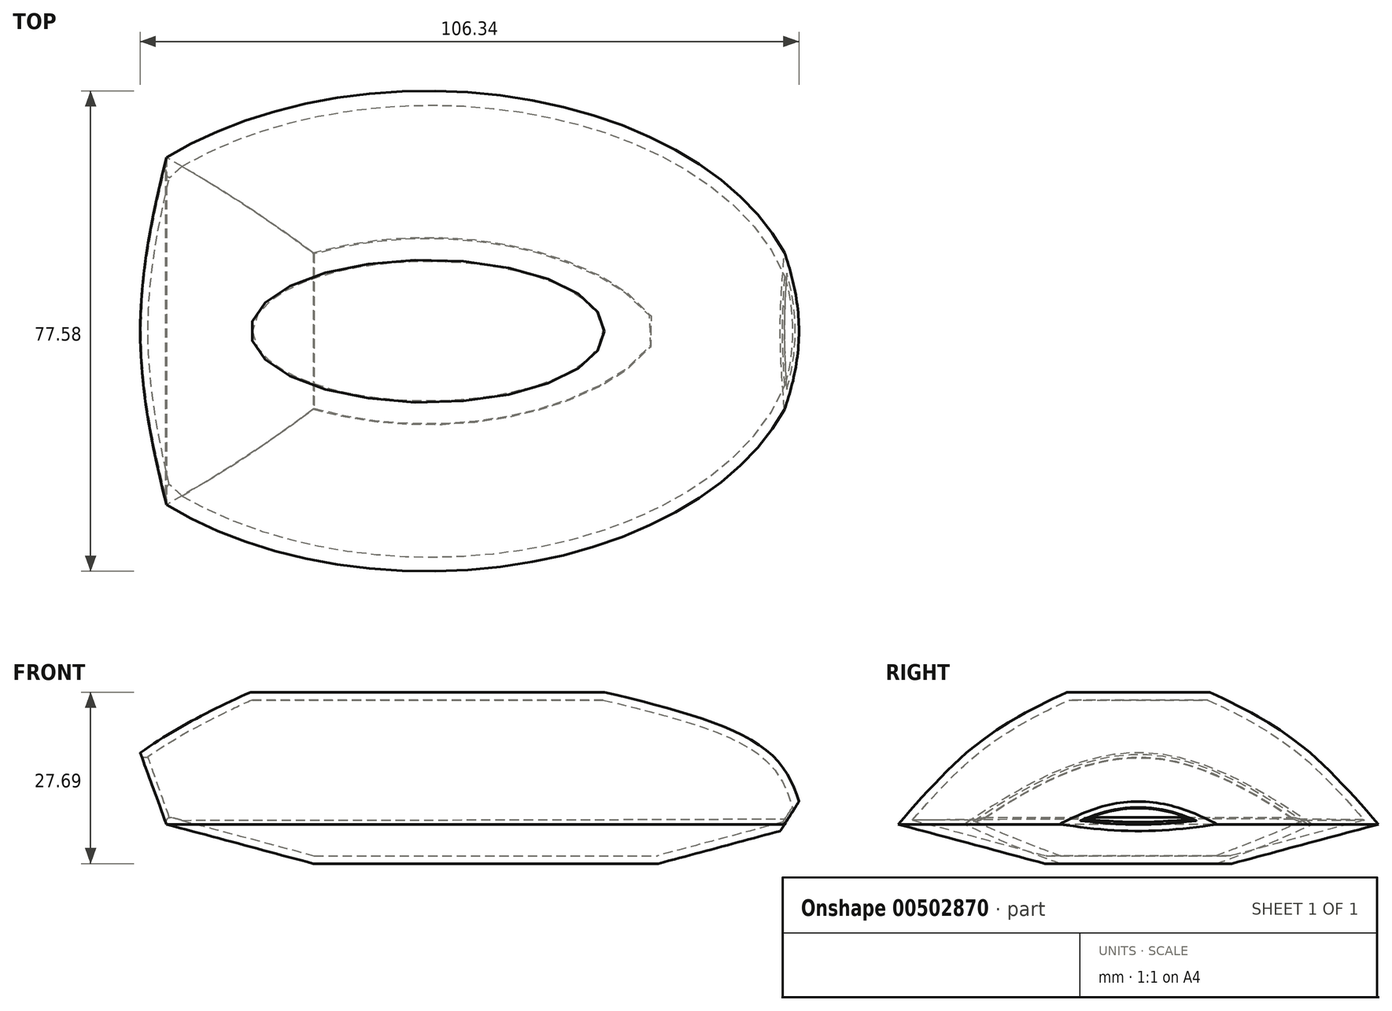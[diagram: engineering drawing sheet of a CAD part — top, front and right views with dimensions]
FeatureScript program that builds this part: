
annotation { "Feature Type Name" : "Feature", "Feature Type Description" : "" }
export const myFeature = defineFeature(function(context is Context, id is Id, definition is map)
    precondition{}
    {
        {
            var Q0;
            Q0=qCreatedBy(makeId("Top.planeOp"),FACE);
            var sketch = newSketch(context, id + "F0", { "sketchPlane" : qUnion([Q0])});
            skEllipse(sketch, "E0", {"center": v(0, 0) * mm, "majorRadius": 60.99 * mm, "minorRadius": 38.8 * mm, "majorAxis": v(1, 0)});
            skSolve(sketch);
        }
        {
            var Q0;
            Q0=qCreatedBy(makeId("Top.planeOp"),FACE);
            cPlane(context, id + "F1", {"entities" : qUnion([Q0]), "cplaneType" : CPlaneType.OFFSET, "offset" : 11.43 * mm, "width" : 152.4 * mm, "height" : 152.4 * mm});
        }
        {
            var Q0;
            Q0=qCreatedBy(id+"F1.planeOp",FACE);
            var sketch = newSketch(context, id + "F2", { "sketchPlane" : qUnion([Q0])});
            skEllipse(sketch, "E1", {"center": v(4.4, 0) * mm, "majorRadius": 50.93 * mm, "minorRadius": 27.86 * mm, "majorAxis": v(1, 0)});
            skSolve(sketch);
        }
        {
            var Q0;
            Q0=qCreatedBy(id+"F1.planeOp",FACE);
            cPlane(context, id + "F3", {"entities" : qUnion([Q0]), "cplaneType" : CPlaneType.OFFSET, "offset" : 9.9 * mm, "width" : 152.4 * mm, "height" : 152.4 * mm});
        }
        {
            var Q0;
            Q0=qCreatedBy(id+"F3.planeOp",FACE);
            var sketch = newSketch(context, id + "F4", { "sketchPlane" : qUnion([Q0])});
            skEllipse(sketch, "E2", {"center": v(0, 0) * mm, "majorRadius": 28.55 * mm, "minorRadius": 11.52 * mm, "majorAxis": v(1, 0)});
            skSolve(sketch);
        }
        {
            var Q0;
            Q0=makeQuery(id+"F0.imprint","IMPRINT",FACE,{"disambiguationData":[TD([[makeQuery(id+"F0.imprint","IMPRINT",EDGE,{"derivedFrom":sQuery(id+"F0.wireOp",EDGE,"E0")}),1.0]])]});
            var Q1;
            Q1=makeQuery(id+"F2.imprint","IMPRINT",FACE,{"disambiguationData":[TD([[makeQuery(id+"F2.imprint","IMPRINT",EDGE,{"derivedFrom":sQuery(id+"F2.wireOp",EDGE,"E1")}),1.0]])]});
            var Q2;
            Q2=makeQuery(id+"F4.imprint","IMPRINT",FACE,{"disambiguationData":[TD([[makeQuery(id+"F4.imprint","IMPRINT",EDGE,{"derivedFrom":sQuery(id+"F4.wireOp",EDGE,"E2")}),1.0]])]});
            loft(context, id + "F5", {"sheetProfilesArray" : [{ "sheetProfileEntities" : qUnion([Q0]) }, { "sheetProfileEntities" : qUnion([Q1]) }, { "sheetProfileEntities" : qUnion([Q2]) }]});
        }
        {
            var Q0;
            Q0=qCreatedBy(makeId("Front.planeOp"),FACE);
            var sketch = newSketch(context, id + "F6", { "sketchPlane" : qUnion([Q0])});
            skLineSegment(sketch, "E3", {"start": v(-50.93, 24.05) * mm, "end": v(-38.98, -8.65) * mm});
            skLineSegment(sketch, "E4", {"start": v(-38.98, -8.65) * mm, "end": v(-67.9, -14.93) * mm});
            skLineSegment(sketch, "E5", {"start": v(-67.9, -14.93) * mm, "end": v(-64.13, 29.08) * mm});
            skLineSegment(sketch, "E6", {"start": v(-64.13, 29.08) * mm, "end": v(-50.93, 24.05) * mm});
            skSolve(sketch);
        }
        {
            var Q0;
            Q0 = qSketchRegion(id + "F6", true);
            extrude(context, id + "F7", {"entities" : qUnion([Q0]), "operationType" : NewBodyOperationType.REMOVE, "endBound" : BoundingType.SYMMETRIC, "oppositeDirection" : true, "depth" : 172.72 * mm, "offsetDistance" : 25.4 * mm});
        }
        {
            var Q0;
            Q0=makeQuery(id+"F5.opLoft","CAP_FACE",FACE,{"disambiguationData":[OSD([makeQuery(id+"F0.imprint","IMPRINT",FACE,{"disambiguationData":[TD([[makeQuery(id+"F0.imprint","IMPRINT",EDGE,{"derivedFrom":sQuery(id+"F0.wireOp",EDGE,"E0")}),1.0]])]})])],"isStart":true});
            extrude(context, id + "F8", {"entities" : qUnion([Q0]), "operationType" : NewBodyOperationType.ADD, "depth" : 6.35 * mm, "offsetDistance" : 25.4 * mm, "hasDraft" : true, "draftAngle" : 75 * degree, "draftPullDirection" : true});
        }
        {
            var Q0;
            Q0=qCreatedBy(makeId("Front.planeOp"),FACE);
            var sketch = newSketch(context, id + "F9", { "sketchPlane" : qUnion([Q0])});
            skLineSegment(sketch, "E7", {"start": v(64.03, 10.07) * mm, "end": v(51.06, -10.4) * mm});
            skLineSegment(sketch, "E8", {"start": v(51.06, -10.4) * mm, "end": v(65.19, -14.72) * mm});
            skLineSegment(sketch, "E9", {"start": v(65.19, -14.72) * mm, "end": v(64.03, 10.07) * mm});
            skSolve(sketch);
        }
        {
            var Q0;
            Q0 = qSketchRegion(id + "F9", true);
            extrude(context, id + "F10", {"entities" : qUnion([Q0]), "operationType" : NewBodyOperationType.REMOVE, "endBound" : BoundingType.SYMMETRIC, "oppositeDirection" : true, "depth" : 77.22 * mm, "offsetDistance" : 25.4 * mm});
        }
        {
            var Q0;
            Q0=makeQuery(id+"F7.boolean.opBoolean","COPY",FACE,{"derivedFrom":makeQuery(id+"F7.opExtrude","SWEPT_FACE",FACE,{"disambiguationData":[OSD([sQuery(id+"F6.wireOp",EDGE,"E3")])]})});
            var Q1;
            Q1=makeQuery(id+"F10.boolean.opBoolean","COPY",FACE,{"derivedFrom":makeQuery(id+"F10.opExtrude","SWEPT_FACE",FACE,{"disambiguationData":[OSD([sQuery(id+"F9.wireOp",EDGE,"E7")])]})});
            shell(context, id + "F11", {"entities" : qUnion([Q0, Q1]), "thickness" : 1.27 * mm});
        }
        {
            var Q0;
            Q0=makeQuery(id+"F11.opShell","OFFSET_EDGE",EDGE,{"disambiguationData":[OSD([sQuery(id+"F0.wireOp",EDGE,"E0"),sQuery(id+"F2.wireOp",EDGE,"E1"),sQuery(id+"F9.wireOp",EDGE,"E7")])]});
            var Q1;
            Q1=makeQuery(id+"F11.opShell","OFFSET_EDGE",EDGE,{"disambiguationData":[OSD([sQuery(id+"F0.wireOp",EDGE,"E0"),sQuery(id+"F9.wireOp",EDGE,"E7")])]});
            fillet(context, id + "F12", {"entities" : qUnion([Q0, Q1]), "radius" : 0.25 * mm, "tangentPropagation" : true, "allowEdgeOverflow" : false});
        }
        {
            var Q0;
            Q0=makeQuery(id+"F11.opShell","OFFSET_EDGE",EDGE,{"disambiguationData":[OSD([sQuery(id+"F0.wireOp",EDGE,"E0"),sQuery(id+"F2.wireOp",EDGE,"E1"),sQuery(id+"F6.wireOp",EDGE,"E3")])]});
            var Q1;
            {var subQ0=sQuery(id+"F6.wireOp",EDGE,"E3");var subQ1=makeQuery(id+"F0.imprint","IMPRINT",FACE,{"disambiguationData":[TD([[makeQuery(id+"F0.imprint","IMPRINT",EDGE,{"derivedFrom":sQuery(id+"F0.wireOp",EDGE,"E0")}),1.0]])]});Q1=makeQuery(id+"F11.opShell","OFFSET_EDGE",EDGE,{"disambiguationData":[OSD([subQ1,subQ0]),TDD([makeQuery(id+"F8.boolean.opBoolean","MERGE",EDGE,{"derivedFrom":[makeQuery(id+"F7.boolean.opBoolean","INTERSECT",EDGE,{"derivedFrom":[makeQuery(id+"F5.opLoft","CAP_FACE",FACE,{"disambiguationData":[OSD([subQ1])],"isStart":true}),makeQuery(id+"F7.opExtrude","SWEPT_FACE",FACE,{"disambiguationData":[OSD([subQ0])]})]}),makeQuery(id+"F8.opExtrude","CAP_EDGE",EDGE,{"disambiguationData":[OSD([subQ1,subQ0])],"isStart":true})]})])]});}
            fillet(context, id + "F13", {"entities" : qUnion([Q0, Q1]), "radius" : 0.76 * mm, "tangentPropagation" : true, "allowEdgeOverflow" : false});
        }
    });
